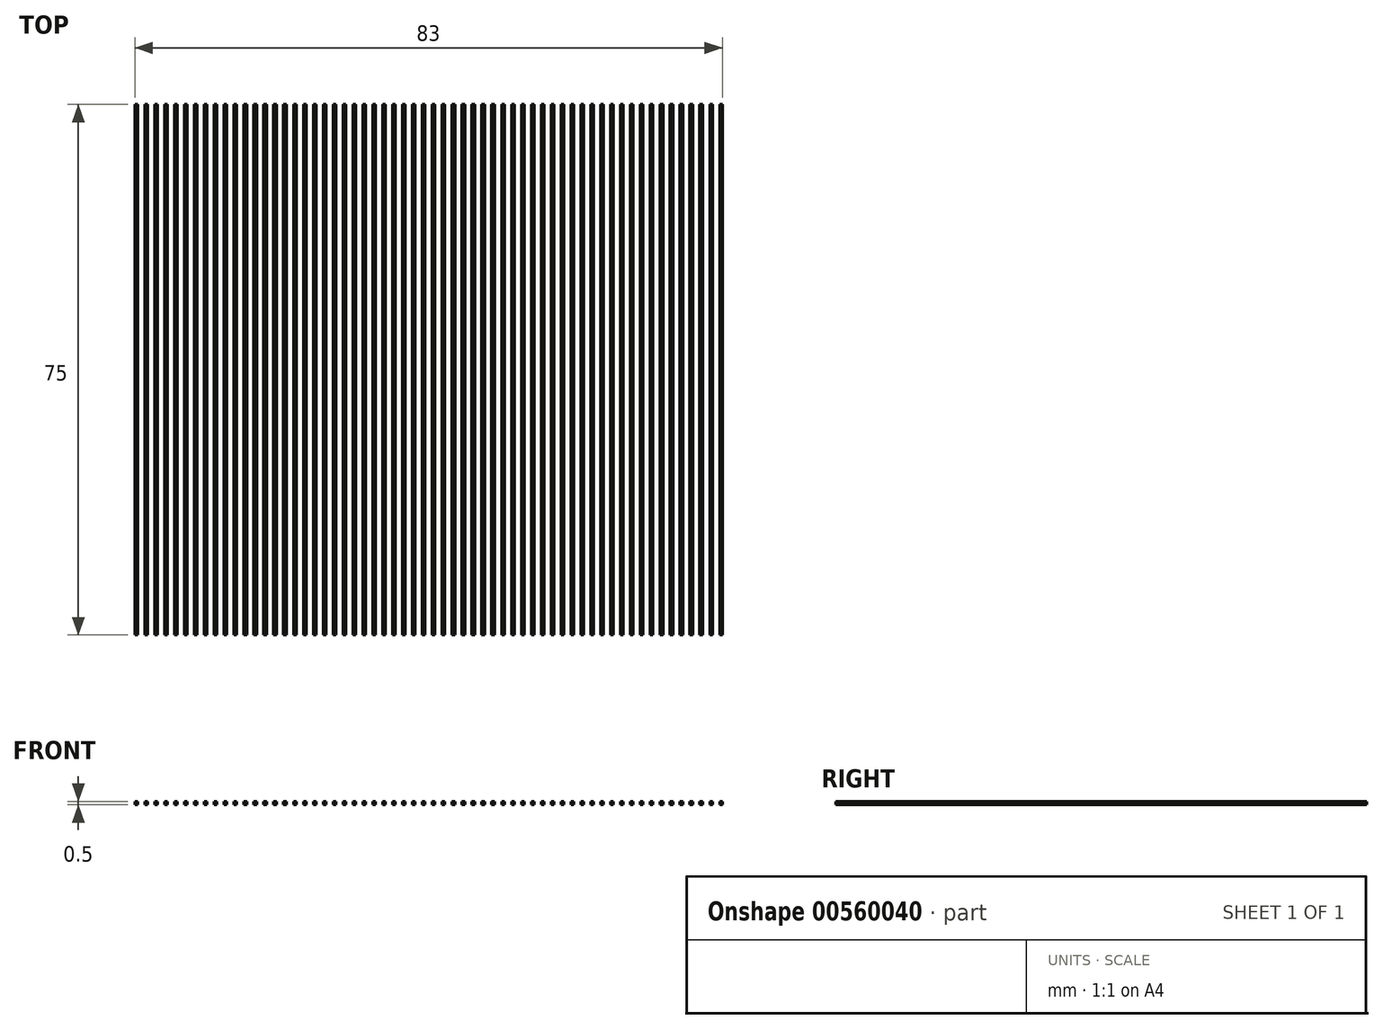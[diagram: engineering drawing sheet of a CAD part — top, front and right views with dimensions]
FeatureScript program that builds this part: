
annotation { "Feature Type Name" : "Feature", "Feature Type Description" : "" }
export const myFeature = defineFeature(function(context is Context, id is Id, definition is map)
    precondition{}
    {
        {
            var Q0;
            Q0=qCreatedBy(makeId("Top.planeOp"),FACE);
            var sketch = newSketch(context, id + "F0", { "sketchPlane" : qUnion([Q0])});
            skLineSegment(sketch, "E0.bottom", {"start": v(-41.94, 37.5) * mm, "end": v(-42.34, 37.5) * mm});
            skLineSegment(sketch, "E0.top", {"start": v(-41.94, -37.5) * mm, "end": v(-42.34, -37.5) * mm});
            skLineSegment(sketch, "E0.left", {"start": v(-41.94, 37.5) * mm, "end": v(-41.94, -37.5) * mm});
            skLineSegment(sketch, "E0.right", {"start": v(-42.34, 37.5) * mm, "end": v(-42.34, -37.5) * mm});
            skPoint(sketch, "E0.middle", {"position": v(-42.14, 0) * mm});
            skLineSegment(sketch, "E1.1.0.0", {"start": v(-40.94, 37.5) * mm, "end": v(-40.94, -37.5) * mm});
            skPoint(sketch, "E1.1.0.1", {"position": v(-40.74, 0) * mm});
            skLineSegment(sketch, "E1.1.0.2", {"start": v(-40.54, 37.5) * mm, "end": v(-40.54, -37.5) * mm});
            skLineSegment(sketch, "E1.1.0.3", {"start": v(-40.54, -37.5) * mm, "end": v(-40.94, -37.5) * mm});
            skLineSegment(sketch, "E1.1.0.4", {"start": v(-40.54, 37.5) * mm, "end": v(-40.94, 37.5) * mm});
            skLineSegment(sketch, "E1.2.0.0", {"start": v(-39.54, 37.5) * mm, "end": v(-39.54, -37.5) * mm});
            skPoint(sketch, "E1.2.0.1", {"position": v(-39.34, 0) * mm});
            skLineSegment(sketch, "E1.2.0.2", {"start": v(-39.14, 37.5) * mm, "end": v(-39.14, -37.5) * mm});
            skLineSegment(sketch, "E1.2.0.3", {"start": v(-39.14, -37.5) * mm, "end": v(-39.54, -37.5) * mm});
            skLineSegment(sketch, "E1.2.0.4", {"start": v(-39.14, 37.5) * mm, "end": v(-39.54, 37.5) * mm});
            skLineSegment(sketch, "E1.3.0.0", {"start": v(-38.14, 37.5) * mm, "end": v(-38.14, -37.5) * mm});
            skPoint(sketch, "E1.3.0.1", {"position": v(-37.94, 0) * mm});
            skLineSegment(sketch, "E1.3.0.2", {"start": v(-37.74, 37.5) * mm, "end": v(-37.74, -37.5) * mm});
            skLineSegment(sketch, "E1.3.0.3", {"start": v(-37.74, -37.5) * mm, "end": v(-38.14, -37.5) * mm});
            skLineSegment(sketch, "E1.3.0.4", {"start": v(-37.74, 37.5) * mm, "end": v(-38.14, 37.5) * mm});
            skLineSegment(sketch, "E1.4.0.0", {"start": v(-36.74, 37.5) * mm, "end": v(-36.74, -37.5) * mm});
            skPoint(sketch, "E1.4.0.1", {"position": v(-36.54, 0) * mm});
            skLineSegment(sketch, "E1.4.0.2", {"start": v(-36.34, 37.5) * mm, "end": v(-36.34, -37.5) * mm});
            skLineSegment(sketch, "E1.4.0.3", {"start": v(-36.34, -37.5) * mm, "end": v(-36.74, -37.5) * mm});
            skLineSegment(sketch, "E1.4.0.4", {"start": v(-36.34, 37.5) * mm, "end": v(-36.74, 37.5) * mm});
            skLineSegment(sketch, "E1.5.0.0", {"start": v(-35.34, 37.5) * mm, "end": v(-35.34, -37.5) * mm});
            skPoint(sketch, "E1.5.0.1", {"position": v(-35.14, 0) * mm});
            skLineSegment(sketch, "E1.5.0.2", {"start": v(-34.94, 37.5) * mm, "end": v(-34.94, -37.5) * mm});
            skLineSegment(sketch, "E1.5.0.3", {"start": v(-34.94, -37.5) * mm, "end": v(-35.34, -37.5) * mm});
            skLineSegment(sketch, "E1.5.0.4", {"start": v(-34.94, 37.5) * mm, "end": v(-35.34, 37.5) * mm});
            skLineSegment(sketch, "E1.6.0.0", {"start": v(-33.94, 37.5) * mm, "end": v(-33.94, -37.5) * mm});
            skPoint(sketch, "E1.6.0.1", {"position": v(-33.74, 0) * mm});
            skLineSegment(sketch, "E1.6.0.2", {"start": v(-33.54, 37.5) * mm, "end": v(-33.54, -37.5) * mm});
            skLineSegment(sketch, "E1.6.0.3", {"start": v(-33.54, -37.5) * mm, "end": v(-33.94, -37.5) * mm});
            skLineSegment(sketch, "E1.6.0.4", {"start": v(-33.54, 37.5) * mm, "end": v(-33.94, 37.5) * mm});
            skLineSegment(sketch, "E1.7.0.0", {"start": v(-32.54, 37.5) * mm, "end": v(-32.54, -37.5) * mm});
            skPoint(sketch, "E1.7.0.1", {"position": v(-32.34, 0) * mm});
            skLineSegment(sketch, "E1.7.0.2", {"start": v(-32.14, 37.5) * mm, "end": v(-32.14, -37.5) * mm});
            skLineSegment(sketch, "E1.7.0.3", {"start": v(-32.14, -37.5) * mm, "end": v(-32.54, -37.5) * mm});
            skLineSegment(sketch, "E1.7.0.4", {"start": v(-32.14, 37.5) * mm, "end": v(-32.54, 37.5) * mm});
            skLineSegment(sketch, "E1.8.0.0", {"start": v(-31.14, 37.5) * mm, "end": v(-31.14, -37.5) * mm});
            skPoint(sketch, "E1.8.0.1", {"position": v(-30.94, 0) * mm});
            skLineSegment(sketch, "E1.8.0.2", {"start": v(-30.74, 37.5) * mm, "end": v(-30.74, -37.5) * mm});
            skLineSegment(sketch, "E1.8.0.3", {"start": v(-30.74, -37.5) * mm, "end": v(-31.14, -37.5) * mm});
            skLineSegment(sketch, "E1.8.0.4", {"start": v(-30.74, 37.5) * mm, "end": v(-31.14, 37.5) * mm});
            skLineSegment(sketch, "E1.9.0.0", {"start": v(-29.74, 37.5) * mm, "end": v(-29.74, -37.5) * mm});
            skPoint(sketch, "E1.9.0.1", {"position": v(-29.54, 0) * mm});
            skLineSegment(sketch, "E1.9.0.2", {"start": v(-29.34, 37.5) * mm, "end": v(-29.34, -37.5) * mm});
            skLineSegment(sketch, "E1.9.0.3", {"start": v(-29.34, -37.5) * mm, "end": v(-29.74, -37.5) * mm});
            skLineSegment(sketch, "E1.9.0.4", {"start": v(-29.34, 37.5) * mm, "end": v(-29.74, 37.5) * mm});
            skLineSegment(sketch, "E1.10.0.0", {"start": v(-28.34, 37.5) * mm, "end": v(-28.34, -37.5) * mm});
            skPoint(sketch, "E1.10.0.1", {"position": v(-28.14, 0) * mm});
            skLineSegment(sketch, "E1.10.0.2", {"start": v(-27.94, 37.5) * mm, "end": v(-27.94, -37.5) * mm});
            skLineSegment(sketch, "E1.10.0.3", {"start": v(-27.94, -37.5) * mm, "end": v(-28.34, -37.5) * mm});
            skLineSegment(sketch, "E1.10.0.4", {"start": v(-27.94, 37.5) * mm, "end": v(-28.34, 37.5) * mm});
            skLineSegment(sketch, "E1.11.0.0", {"start": v(-26.94, 37.5) * mm, "end": v(-26.94, -37.5) * mm});
            skPoint(sketch, "E1.11.0.1", {"position": v(-26.74, 0) * mm});
            skLineSegment(sketch, "E1.11.0.2", {"start": v(-26.54, 37.5) * mm, "end": v(-26.54, -37.5) * mm});
            skLineSegment(sketch, "E1.11.0.3", {"start": v(-26.54, -37.5) * mm, "end": v(-26.94, -37.5) * mm});
            skLineSegment(sketch, "E1.11.0.4", {"start": v(-26.54, 37.5) * mm, "end": v(-26.94, 37.5) * mm});
            skLineSegment(sketch, "E1.12.0.0", {"start": v(-25.54, 37.5) * mm, "end": v(-25.54, -37.5) * mm});
            skPoint(sketch, "E1.12.0.1", {"position": v(-25.34, 0) * mm});
            skLineSegment(sketch, "E1.12.0.2", {"start": v(-25.14, 37.5) * mm, "end": v(-25.14, -37.5) * mm});
            skLineSegment(sketch, "E1.12.0.3", {"start": v(-25.14, -37.5) * mm, "end": v(-25.54, -37.5) * mm});
            skLineSegment(sketch, "E1.12.0.4", {"start": v(-25.14, 37.5) * mm, "end": v(-25.54, 37.5) * mm});
            skLineSegment(sketch, "E1.13.0.0", {"start": v(-24.14, 37.5) * mm, "end": v(-24.14, -37.5) * mm});
            skPoint(sketch, "E1.13.0.1", {"position": v(-23.94, 0) * mm});
            skLineSegment(sketch, "E1.13.0.2", {"start": v(-23.74, 37.5) * mm, "end": v(-23.74, -37.5) * mm});
            skLineSegment(sketch, "E1.13.0.3", {"start": v(-23.74, -37.5) * mm, "end": v(-24.14, -37.5) * mm});
            skLineSegment(sketch, "E1.13.0.4", {"start": v(-23.74, 37.5) * mm, "end": v(-24.14, 37.5) * mm});
            skLineSegment(sketch, "E1.14.0.0", {"start": v(-22.74, 37.5) * mm, "end": v(-22.74, -37.5) * mm});
            skPoint(sketch, "E1.14.0.1", {"position": v(-22.54, 0) * mm});
            skLineSegment(sketch, "E1.14.0.2", {"start": v(-22.34, 37.5) * mm, "end": v(-22.34, -37.5) * mm});
            skLineSegment(sketch, "E1.14.0.3", {"start": v(-22.34, -37.5) * mm, "end": v(-22.74, -37.5) * mm});
            skLineSegment(sketch, "E1.14.0.4", {"start": v(-22.34, 37.5) * mm, "end": v(-22.74, 37.5) * mm});
            skLineSegment(sketch, "E1.15.0.0", {"start": v(-21.34, 37.5) * mm, "end": v(-21.34, -37.5) * mm});
            skPoint(sketch, "E1.15.0.1", {"position": v(-21.14, 0) * mm});
            skLineSegment(sketch, "E1.15.0.2", {"start": v(-20.94, 37.5) * mm, "end": v(-20.94, -37.5) * mm});
            skLineSegment(sketch, "E1.15.0.3", {"start": v(-20.94, -37.5) * mm, "end": v(-21.34, -37.5) * mm});
            skLineSegment(sketch, "E1.15.0.4", {"start": v(-20.94, 37.5) * mm, "end": v(-21.34, 37.5) * mm});
            skLineSegment(sketch, "E1.16.0.0", {"start": v(-19.94, 37.5) * mm, "end": v(-19.94, -37.5) * mm});
            skPoint(sketch, "E1.16.0.1", {"position": v(-19.74, 0) * mm});
            skLineSegment(sketch, "E1.16.0.2", {"start": v(-19.54, 37.5) * mm, "end": v(-19.54, -37.5) * mm});
            skLineSegment(sketch, "E1.16.0.3", {"start": v(-19.54, -37.5) * mm, "end": v(-19.94, -37.5) * mm});
            skLineSegment(sketch, "E1.16.0.4", {"start": v(-19.54, 37.5) * mm, "end": v(-19.94, 37.5) * mm});
            skLineSegment(sketch, "E1.17.0.0", {"start": v(-18.54, 37.5) * mm, "end": v(-18.54, -37.5) * mm});
            skPoint(sketch, "E1.17.0.1", {"position": v(-18.34, 0) * mm});
            skLineSegment(sketch, "E1.17.0.2", {"start": v(-18.14, 37.5) * mm, "end": v(-18.14, -37.5) * mm});
            skLineSegment(sketch, "E1.17.0.3", {"start": v(-18.14, -37.5) * mm, "end": v(-18.54, -37.5) * mm});
            skLineSegment(sketch, "E1.17.0.4", {"start": v(-18.14, 37.5) * mm, "end": v(-18.54, 37.5) * mm});
            skLineSegment(sketch, "E1.18.0.0", {"start": v(-17.14, 37.5) * mm, "end": v(-17.14, -37.5) * mm});
            skPoint(sketch, "E1.18.0.1", {"position": v(-16.94, 0) * mm});
            skLineSegment(sketch, "E1.18.0.2", {"start": v(-16.74, 37.5) * mm, "end": v(-16.74, -37.5) * mm});
            skLineSegment(sketch, "E1.18.0.3", {"start": v(-16.74, -37.5) * mm, "end": v(-17.14, -37.5) * mm});
            skLineSegment(sketch, "E1.18.0.4", {"start": v(-16.74, 37.5) * mm, "end": v(-17.14, 37.5) * mm});
            skLineSegment(sketch, "E1.19.0.0", {"start": v(-15.74, 37.5) * mm, "end": v(-15.74, -37.5) * mm});
            skPoint(sketch, "E1.19.0.1", {"position": v(-15.54, 0) * mm});
            skLineSegment(sketch, "E1.19.0.2", {"start": v(-15.34, 37.5) * mm, "end": v(-15.34, -37.5) * mm});
            skLineSegment(sketch, "E1.19.0.3", {"start": v(-15.34, -37.5) * mm, "end": v(-15.74, -37.5) * mm});
            skLineSegment(sketch, "E1.19.0.4", {"start": v(-15.34, 37.5) * mm, "end": v(-15.74, 37.5) * mm});
            skLineSegment(sketch, "E1.20.0.0", {"start": v(-14.34, 37.5) * mm, "end": v(-14.34, -37.5) * mm});
            skPoint(sketch, "E1.20.0.1", {"position": v(-14.14, 0) * mm});
            skLineSegment(sketch, "E1.20.0.2", {"start": v(-13.94, 37.5) * mm, "end": v(-13.94, -37.5) * mm});
            skLineSegment(sketch, "E1.20.0.3", {"start": v(-13.94, -37.5) * mm, "end": v(-14.34, -37.5) * mm});
            skLineSegment(sketch, "E1.20.0.4", {"start": v(-13.94, 37.5) * mm, "end": v(-14.34, 37.5) * mm});
            skLineSegment(sketch, "E1.21.0.0", {"start": v(-12.94, 37.5) * mm, "end": v(-12.94, -37.5) * mm});
            skPoint(sketch, "E1.21.0.1", {"position": v(-12.74, 0) * mm});
            skLineSegment(sketch, "E1.21.0.2", {"start": v(-12.54, 37.5) * mm, "end": v(-12.54, -37.5) * mm});
            skLineSegment(sketch, "E1.21.0.3", {"start": v(-12.54, -37.5) * mm, "end": v(-12.94, -37.5) * mm});
            skLineSegment(sketch, "E1.21.0.4", {"start": v(-12.54, 37.5) * mm, "end": v(-12.94, 37.5) * mm});
            skLineSegment(sketch, "E1.22.0.0", {"start": v(-11.54, 37.5) * mm, "end": v(-11.54, -37.5) * mm});
            skPoint(sketch, "E1.22.0.1", {"position": v(-11.34, 0) * mm});
            skLineSegment(sketch, "E1.22.0.2", {"start": v(-11.14, 37.5) * mm, "end": v(-11.14, -37.5) * mm});
            skLineSegment(sketch, "E1.22.0.3", {"start": v(-11.14, -37.5) * mm, "end": v(-11.54, -37.5) * mm});
            skLineSegment(sketch, "E1.22.0.4", {"start": v(-11.14, 37.5) * mm, "end": v(-11.54, 37.5) * mm});
            skLineSegment(sketch, "E1.23.0.0", {"start": v(-10.14, 37.5) * mm, "end": v(-10.14, -37.5) * mm});
            skPoint(sketch, "E1.23.0.1", {"position": v(-9.94, 0) * mm});
            skLineSegment(sketch, "E1.23.0.2", {"start": v(-9.74, 37.5) * mm, "end": v(-9.74, -37.5) * mm});
            skLineSegment(sketch, "E1.23.0.3", {"start": v(-9.74, -37.5) * mm, "end": v(-10.14, -37.5) * mm});
            skLineSegment(sketch, "E1.23.0.4", {"start": v(-9.74, 37.5) * mm, "end": v(-10.14, 37.5) * mm});
            skLineSegment(sketch, "E1.24.0.0", {"start": v(-8.74, 37.5) * mm, "end": v(-8.74, -37.5) * mm});
            skPoint(sketch, "E1.24.0.1", {"position": v(-8.54, 0) * mm});
            skLineSegment(sketch, "E1.24.0.2", {"start": v(-8.34, 37.5) * mm, "end": v(-8.34, -37.5) * mm});
            skLineSegment(sketch, "E1.24.0.3", {"start": v(-8.34, -37.5) * mm, "end": v(-8.74, -37.5) * mm});
            skLineSegment(sketch, "E1.24.0.4", {"start": v(-8.34, 37.5) * mm, "end": v(-8.74, 37.5) * mm});
            skLineSegment(sketch, "E1.25.0.0", {"start": v(-7.34, 37.5) * mm, "end": v(-7.34, -37.5) * mm});
            skPoint(sketch, "E1.25.0.1", {"position": v(-7.14, 0) * mm});
            skLineSegment(sketch, "E1.25.0.2", {"start": v(-6.94, 37.5) * mm, "end": v(-6.94, -37.5) * mm});
            skLineSegment(sketch, "E1.25.0.3", {"start": v(-6.94, -37.5) * mm, "end": v(-7.34, -37.5) * mm});
            skLineSegment(sketch, "E1.25.0.4", {"start": v(-6.94, 37.5) * mm, "end": v(-7.34, 37.5) * mm});
            skLineSegment(sketch, "E1.26.0.0", {"start": v(-5.94, 37.5) * mm, "end": v(-5.94, -37.5) * mm});
            skPoint(sketch, "E1.26.0.1", {"position": v(-5.74, 0) * mm});
            skLineSegment(sketch, "E1.26.0.2", {"start": v(-5.54, 37.5) * mm, "end": v(-5.54, -37.5) * mm});
            skLineSegment(sketch, "E1.26.0.3", {"start": v(-5.54, -37.5) * mm, "end": v(-5.94, -37.5) * mm});
            skLineSegment(sketch, "E1.26.0.4", {"start": v(-5.54, 37.5) * mm, "end": v(-5.94, 37.5) * mm});
            skLineSegment(sketch, "E1.27.0.0", {"start": v(-4.54, 37.5) * mm, "end": v(-4.54, -37.5) * mm});
            skPoint(sketch, "E1.27.0.1", {"position": v(-4.34, 0) * mm});
            skLineSegment(sketch, "E1.27.0.2", {"start": v(-4.14, 37.5) * mm, "end": v(-4.14, -37.5) * mm});
            skLineSegment(sketch, "E1.27.0.3", {"start": v(-4.14, -37.5) * mm, "end": v(-4.54, -37.5) * mm});
            skLineSegment(sketch, "E1.27.0.4", {"start": v(-4.14, 37.5) * mm, "end": v(-4.54, 37.5) * mm});
            skLineSegment(sketch, "E1.28.0.0", {"start": v(-3.14, 37.5) * mm, "end": v(-3.14, -37.5) * mm});
            skPoint(sketch, "E1.28.0.1", {"position": v(-2.94, 0) * mm});
            skLineSegment(sketch, "E1.28.0.2", {"start": v(-2.74, 37.5) * mm, "end": v(-2.74, -37.5) * mm});
            skLineSegment(sketch, "E1.28.0.3", {"start": v(-2.74, -37.5) * mm, "end": v(-3.14, -37.5) * mm});
            skLineSegment(sketch, "E1.28.0.4", {"start": v(-2.74, 37.5) * mm, "end": v(-3.14, 37.5) * mm});
            skLineSegment(sketch, "E1.29.0.0", {"start": v(-1.74, 37.5) * mm, "end": v(-1.74, -37.5) * mm});
            skPoint(sketch, "E1.29.0.1", {"position": v(-1.54, 0) * mm});
            skLineSegment(sketch, "E1.29.0.2", {"start": v(-1.34, 37.5) * mm, "end": v(-1.34, -37.5) * mm});
            skLineSegment(sketch, "E1.29.0.3", {"start": v(-1.34, -37.5) * mm, "end": v(-1.74, -37.5) * mm});
            skLineSegment(sketch, "E1.29.0.4", {"start": v(-1.34, 37.5) * mm, "end": v(-1.74, 37.5) * mm});
            skLineSegment(sketch, "E1.30.0.0", {"start": v(-0.34, 37.5) * mm, "end": v(-0.34, -37.5) * mm});
            skPoint(sketch, "E1.30.0.1", {"position": v(-0.14, 0) * mm});
            skLineSegment(sketch, "E1.30.0.2", {"start": v(0.06, 37.5) * mm, "end": v(0.06, -37.5) * mm});
            skLineSegment(sketch, "E1.30.0.3", {"start": v(0.06, -37.5) * mm, "end": v(-0.34, -37.5) * mm});
            skLineSegment(sketch, "E1.30.0.4", {"start": v(0.06, 37.5) * mm, "end": v(-0.34, 37.5) * mm});
            skLineSegment(sketch, "E1.31.0.0", {"start": v(1.06, 37.5) * mm, "end": v(1.06, -37.5) * mm});
            skPoint(sketch, "E1.31.0.1", {"position": v(1.26, 0) * mm});
            skLineSegment(sketch, "E1.31.0.2", {"start": v(1.46, 37.5) * mm, "end": v(1.46, -37.5) * mm});
            skLineSegment(sketch, "E1.31.0.3", {"start": v(1.46, -37.5) * mm, "end": v(1.06, -37.5) * mm});
            skLineSegment(sketch, "E1.31.0.4", {"start": v(1.46, 37.5) * mm, "end": v(1.06, 37.5) * mm});
            skLineSegment(sketch, "E1.32.0.0", {"start": v(2.46, 37.5) * mm, "end": v(2.46, -37.5) * mm});
            skPoint(sketch, "E1.32.0.1", {"position": v(2.66, 0) * mm});
            skLineSegment(sketch, "E1.32.0.2", {"start": v(2.86, 37.5) * mm, "end": v(2.86, -37.5) * mm});
            skLineSegment(sketch, "E1.32.0.3", {"start": v(2.86, -37.5) * mm, "end": v(2.46, -37.5) * mm});
            skLineSegment(sketch, "E1.32.0.4", {"start": v(2.86, 37.5) * mm, "end": v(2.46, 37.5) * mm});
            skLineSegment(sketch, "E1.33.0.0", {"start": v(3.86, 37.5) * mm, "end": v(3.86, -37.5) * mm});
            skPoint(sketch, "E1.33.0.1", {"position": v(4.06, 0) * mm});
            skLineSegment(sketch, "E1.33.0.2", {"start": v(4.26, 37.5) * mm, "end": v(4.26, -37.5) * mm});
            skLineSegment(sketch, "E1.33.0.3", {"start": v(4.26, -37.5) * mm, "end": v(3.86, -37.5) * mm});
            skLineSegment(sketch, "E1.33.0.4", {"start": v(4.26, 37.5) * mm, "end": v(3.86, 37.5) * mm});
            skLineSegment(sketch, "E1.34.0.0", {"start": v(5.26, 37.5) * mm, "end": v(5.26, -37.5) * mm});
            skPoint(sketch, "E1.34.0.1", {"position": v(5.46, 0) * mm});
            skLineSegment(sketch, "E1.34.0.2", {"start": v(5.66, 37.5) * mm, "end": v(5.66, -37.5) * mm});
            skLineSegment(sketch, "E1.34.0.3", {"start": v(5.66, -37.5) * mm, "end": v(5.26, -37.5) * mm});
            skLineSegment(sketch, "E1.34.0.4", {"start": v(5.66, 37.5) * mm, "end": v(5.26, 37.5) * mm});
            skLineSegment(sketch, "E1.35.0.0", {"start": v(6.66, 37.5) * mm, "end": v(6.66, -37.5) * mm});
            skPoint(sketch, "E1.35.0.1", {"position": v(6.86, 0) * mm});
            skLineSegment(sketch, "E1.35.0.2", {"start": v(7.06, 37.5) * mm, "end": v(7.06, -37.5) * mm});
            skLineSegment(sketch, "E1.35.0.3", {"start": v(7.06, -37.5) * mm, "end": v(6.66, -37.5) * mm});
            skLineSegment(sketch, "E1.35.0.4", {"start": v(7.06, 37.5) * mm, "end": v(6.66, 37.5) * mm});
            skLineSegment(sketch, "E1.36.0.0", {"start": v(8.06, 37.5) * mm, "end": v(8.06, -37.5) * mm});
            skPoint(sketch, "E1.36.0.1", {"position": v(8.26, 0) * mm});
            skLineSegment(sketch, "E1.36.0.2", {"start": v(8.46, 37.5) * mm, "end": v(8.46, -37.5) * mm});
            skLineSegment(sketch, "E1.36.0.3", {"start": v(8.46, -37.5) * mm, "end": v(8.06, -37.5) * mm});
            skLineSegment(sketch, "E1.36.0.4", {"start": v(8.46, 37.5) * mm, "end": v(8.06, 37.5) * mm});
            skLineSegment(sketch, "E1.37.0.0", {"start": v(9.46, 37.5) * mm, "end": v(9.46, -37.5) * mm});
            skPoint(sketch, "E1.37.0.1", {"position": v(9.66, 0) * mm});
            skLineSegment(sketch, "E1.37.0.2", {"start": v(9.86, 37.5) * mm, "end": v(9.86, -37.5) * mm});
            skLineSegment(sketch, "E1.37.0.3", {"start": v(9.86, -37.5) * mm, "end": v(9.46, -37.5) * mm});
            skLineSegment(sketch, "E1.37.0.4", {"start": v(9.86, 37.5) * mm, "end": v(9.46, 37.5) * mm});
            skLineSegment(sketch, "E1.38.0.0", {"start": v(10.86, 37.5) * mm, "end": v(10.86, -37.5) * mm});
            skPoint(sketch, "E1.38.0.1", {"position": v(11.06, 0) * mm});
            skLineSegment(sketch, "E1.38.0.2", {"start": v(11.26, 37.5) * mm, "end": v(11.26, -37.5) * mm});
            skLineSegment(sketch, "E1.38.0.3", {"start": v(11.26, -37.5) * mm, "end": v(10.86, -37.5) * mm});
            skLineSegment(sketch, "E1.38.0.4", {"start": v(11.26, 37.5) * mm, "end": v(10.86, 37.5) * mm});
            skLineSegment(sketch, "E1.39.0.0", {"start": v(12.26, 37.5) * mm, "end": v(12.26, -37.5) * mm});
            skPoint(sketch, "E1.39.0.1", {"position": v(12.46, 0) * mm});
            skLineSegment(sketch, "E1.39.0.2", {"start": v(12.66, 37.5) * mm, "end": v(12.66, -37.5) * mm});
            skLineSegment(sketch, "E1.39.0.3", {"start": v(12.66, -37.5) * mm, "end": v(12.26, -37.5) * mm});
            skLineSegment(sketch, "E1.39.0.4", {"start": v(12.66, 37.5) * mm, "end": v(12.26, 37.5) * mm});
            skLineSegment(sketch, "E1.40.0.0", {"start": v(13.66, 37.5) * mm, "end": v(13.66, -37.5) * mm});
            skPoint(sketch, "E1.40.0.1", {"position": v(13.86, 0) * mm});
            skLineSegment(sketch, "E1.40.0.2", {"start": v(14.06, 37.5) * mm, "end": v(14.06, -37.5) * mm});
            skLineSegment(sketch, "E1.40.0.3", {"start": v(14.06, -37.5) * mm, "end": v(13.66, -37.5) * mm});
            skLineSegment(sketch, "E1.40.0.4", {"start": v(14.06, 37.5) * mm, "end": v(13.66, 37.5) * mm});
            skLineSegment(sketch, "E1.41.0.0", {"start": v(15.06, 37.5) * mm, "end": v(15.06, -37.5) * mm});
            skPoint(sketch, "E1.41.0.1", {"position": v(15.26, 0) * mm});
            skLineSegment(sketch, "E1.41.0.2", {"start": v(15.46, 37.5) * mm, "end": v(15.46, -37.5) * mm});
            skLineSegment(sketch, "E1.41.0.3", {"start": v(15.46, -37.5) * mm, "end": v(15.06, -37.5) * mm});
            skLineSegment(sketch, "E1.41.0.4", {"start": v(15.46, 37.5) * mm, "end": v(15.06, 37.5) * mm});
            skLineSegment(sketch, "E1.42.0.0", {"start": v(16.46, 37.5) * mm, "end": v(16.46, -37.5) * mm});
            skPoint(sketch, "E1.42.0.1", {"position": v(16.66, 0) * mm});
            skLineSegment(sketch, "E1.42.0.2", {"start": v(16.86, 37.5) * mm, "end": v(16.86, -37.5) * mm});
            skLineSegment(sketch, "E1.42.0.3", {"start": v(16.86, -37.5) * mm, "end": v(16.46, -37.5) * mm});
            skLineSegment(sketch, "E1.42.0.4", {"start": v(16.86, 37.5) * mm, "end": v(16.46, 37.5) * mm});
            skLineSegment(sketch, "E1.43.0.0", {"start": v(17.86, 37.5) * mm, "end": v(17.86, -37.5) * mm});
            skPoint(sketch, "E1.43.0.1", {"position": v(18.06, 0) * mm});
            skLineSegment(sketch, "E1.43.0.2", {"start": v(18.26, 37.5) * mm, "end": v(18.26, -37.5) * mm});
            skLineSegment(sketch, "E1.43.0.3", {"start": v(18.26, -37.5) * mm, "end": v(17.86, -37.5) * mm});
            skLineSegment(sketch, "E1.43.0.4", {"start": v(18.26, 37.5) * mm, "end": v(17.86, 37.5) * mm});
            skLineSegment(sketch, "E1.44.0.0", {"start": v(19.26, 37.5) * mm, "end": v(19.26, -37.5) * mm});
            skPoint(sketch, "E1.44.0.1", {"position": v(19.46, 0) * mm});
            skLineSegment(sketch, "E1.44.0.2", {"start": v(19.66, 37.5) * mm, "end": v(19.66, -37.5) * mm});
            skLineSegment(sketch, "E1.44.0.3", {"start": v(19.66, -37.5) * mm, "end": v(19.26, -37.5) * mm});
            skLineSegment(sketch, "E1.44.0.4", {"start": v(19.66, 37.5) * mm, "end": v(19.26, 37.5) * mm});
            skLineSegment(sketch, "E1.45.0.0", {"start": v(20.66, 37.5) * mm, "end": v(20.66, -37.5) * mm});
            skPoint(sketch, "E1.45.0.1", {"position": v(20.86, 0) * mm});
            skLineSegment(sketch, "E1.45.0.2", {"start": v(21.06, 37.5) * mm, "end": v(21.06, -37.5) * mm});
            skLineSegment(sketch, "E1.45.0.3", {"start": v(21.06, -37.5) * mm, "end": v(20.66, -37.5) * mm});
            skLineSegment(sketch, "E1.45.0.4", {"start": v(21.06, 37.5) * mm, "end": v(20.66, 37.5) * mm});
            skLineSegment(sketch, "E1.46.0.0", {"start": v(22.06, 37.5) * mm, "end": v(22.06, -37.5) * mm});
            skPoint(sketch, "E1.46.0.1", {"position": v(22.26, 0) * mm});
            skLineSegment(sketch, "E1.46.0.2", {"start": v(22.46, 37.5) * mm, "end": v(22.46, -37.5) * mm});
            skLineSegment(sketch, "E1.46.0.3", {"start": v(22.46, -37.5) * mm, "end": v(22.06, -37.5) * mm});
            skLineSegment(sketch, "E1.46.0.4", {"start": v(22.46, 37.5) * mm, "end": v(22.06, 37.5) * mm});
            skLineSegment(sketch, "E1.47.0.0", {"start": v(23.46, 37.5) * mm, "end": v(23.46, -37.5) * mm});
            skPoint(sketch, "E1.47.0.1", {"position": v(23.66, 0) * mm});
            skLineSegment(sketch, "E1.47.0.2", {"start": v(23.86, 37.5) * mm, "end": v(23.86, -37.5) * mm});
            skLineSegment(sketch, "E1.47.0.3", {"start": v(23.86, -37.5) * mm, "end": v(23.46, -37.5) * mm});
            skLineSegment(sketch, "E1.47.0.4", {"start": v(23.86, 37.5) * mm, "end": v(23.46, 37.5) * mm});
            skLineSegment(sketch, "E1.48.0.0", {"start": v(24.86, 37.5) * mm, "end": v(24.86, -37.5) * mm});
            skPoint(sketch, "E1.48.0.1", {"position": v(25.06, 0) * mm});
            skLineSegment(sketch, "E1.48.0.2", {"start": v(25.26, 37.5) * mm, "end": v(25.26, -37.5) * mm});
            skLineSegment(sketch, "E1.48.0.3", {"start": v(25.26, -37.5) * mm, "end": v(24.86, -37.5) * mm});
            skLineSegment(sketch, "E1.48.0.4", {"start": v(25.26, 37.5) * mm, "end": v(24.86, 37.5) * mm});
            skLineSegment(sketch, "E1.49.0.0", {"start": v(26.26, 37.5) * mm, "end": v(26.26, -37.5) * mm});
            skPoint(sketch, "E1.49.0.1", {"position": v(26.46, 0) * mm});
            skLineSegment(sketch, "E1.49.0.2", {"start": v(26.66, 37.5) * mm, "end": v(26.66, -37.5) * mm});
            skLineSegment(sketch, "E1.49.0.3", {"start": v(26.66, -37.5) * mm, "end": v(26.26, -37.5) * mm});
            skLineSegment(sketch, "E1.49.0.4", {"start": v(26.66, 37.5) * mm, "end": v(26.26, 37.5) * mm});
            skLineSegment(sketch, "E1.50.0.0", {"start": v(27.66, 37.5) * mm, "end": v(27.66, -37.5) * mm});
            skPoint(sketch, "E1.50.0.1", {"position": v(27.86, 0) * mm});
            skLineSegment(sketch, "E1.50.0.2", {"start": v(28.06, 37.5) * mm, "end": v(28.06, -37.5) * mm});
            skLineSegment(sketch, "E1.50.0.3", {"start": v(28.06, -37.5) * mm, "end": v(27.66, -37.5) * mm});
            skLineSegment(sketch, "E1.50.0.4", {"start": v(28.06, 37.5) * mm, "end": v(27.66, 37.5) * mm});
            skLineSegment(sketch, "E1.51.0.0", {"start": v(29.06, 37.5) * mm, "end": v(29.06, -37.5) * mm});
            skPoint(sketch, "E1.51.0.1", {"position": v(29.26, 0) * mm});
            skLineSegment(sketch, "E1.51.0.2", {"start": v(29.46, 37.5) * mm, "end": v(29.46, -37.5) * mm});
            skLineSegment(sketch, "E1.51.0.3", {"start": v(29.46, -37.5) * mm, "end": v(29.06, -37.5) * mm});
            skLineSegment(sketch, "E1.51.0.4", {"start": v(29.46, 37.5) * mm, "end": v(29.06, 37.5) * mm});
            skLineSegment(sketch, "E1.52.0.0", {"start": v(30.46, 37.5) * mm, "end": v(30.46, -37.5) * mm});
            skPoint(sketch, "E1.52.0.1", {"position": v(30.66, 0) * mm});
            skLineSegment(sketch, "E1.52.0.2", {"start": v(30.86, 37.5) * mm, "end": v(30.86, -37.5) * mm});
            skLineSegment(sketch, "E1.52.0.3", {"start": v(30.86, -37.5) * mm, "end": v(30.46, -37.5) * mm});
            skLineSegment(sketch, "E1.52.0.4", {"start": v(30.86, 37.5) * mm, "end": v(30.46, 37.5) * mm});
            skLineSegment(sketch, "E1.53.0.0", {"start": v(31.86, 37.5) * mm, "end": v(31.86, -37.5) * mm});
            skPoint(sketch, "E1.53.0.1", {"position": v(32.06, 0) * mm});
            skLineSegment(sketch, "E1.53.0.2", {"start": v(32.26, 37.5) * mm, "end": v(32.26, -37.5) * mm});
            skLineSegment(sketch, "E1.53.0.3", {"start": v(32.26, -37.5) * mm, "end": v(31.86, -37.5) * mm});
            skLineSegment(sketch, "E1.53.0.4", {"start": v(32.26, 37.5) * mm, "end": v(31.86, 37.5) * mm});
            skLineSegment(sketch, "E1.54.0.0", {"start": v(33.26, 37.5) * mm, "end": v(33.26, -37.5) * mm});
            skPoint(sketch, "E1.54.0.1", {"position": v(33.46, 0) * mm});
            skLineSegment(sketch, "E1.54.0.2", {"start": v(33.66, 37.5) * mm, "end": v(33.66, -37.5) * mm});
            skLineSegment(sketch, "E1.54.0.3", {"start": v(33.66, -37.5) * mm, "end": v(33.26, -37.5) * mm});
            skLineSegment(sketch, "E1.54.0.4", {"start": v(33.66, 37.5) * mm, "end": v(33.26, 37.5) * mm});
            skLineSegment(sketch, "E1.55.0.0", {"start": v(34.66, 37.5) * mm, "end": v(34.66, -37.5) * mm});
            skPoint(sketch, "E1.55.0.1", {"position": v(34.86, 0) * mm});
            skLineSegment(sketch, "E1.55.0.2", {"start": v(35.06, 37.5) * mm, "end": v(35.06, -37.5) * mm});
            skLineSegment(sketch, "E1.55.0.3", {"start": v(35.06, -37.5) * mm, "end": v(34.66, -37.5) * mm});
            skLineSegment(sketch, "E1.55.0.4", {"start": v(35.06, 37.5) * mm, "end": v(34.66, 37.5) * mm});
            skLineSegment(sketch, "E1.56.0.0", {"start": v(36.06, 37.5) * mm, "end": v(36.06, -37.5) * mm});
            skPoint(sketch, "E1.56.0.1", {"position": v(36.26, 0) * mm});
            skLineSegment(sketch, "E1.56.0.2", {"start": v(36.46, 37.5) * mm, "end": v(36.46, -37.5) * mm});
            skLineSegment(sketch, "E1.56.0.3", {"start": v(36.46, -37.5) * mm, "end": v(36.06, -37.5) * mm});
            skLineSegment(sketch, "E1.56.0.4", {"start": v(36.46, 37.5) * mm, "end": v(36.06, 37.5) * mm});
            skLineSegment(sketch, "E1.57.0.0", {"start": v(37.46, 37.5) * mm, "end": v(37.46, -37.5) * mm});
            skPoint(sketch, "E1.57.0.1", {"position": v(37.66, 0) * mm});
            skLineSegment(sketch, "E1.57.0.2", {"start": v(37.86, 37.5) * mm, "end": v(37.86, -37.5) * mm});
            skLineSegment(sketch, "E1.57.0.3", {"start": v(37.86, -37.5) * mm, "end": v(37.46, -37.5) * mm});
            skLineSegment(sketch, "E1.57.0.4", {"start": v(37.86, 37.5) * mm, "end": v(37.46, 37.5) * mm});
            skLineSegment(sketch, "E1.58.0.0", {"start": v(38.86, 37.5) * mm, "end": v(38.86, -37.5) * mm});
            skPoint(sketch, "E1.58.0.1", {"position": v(39.06, 0) * mm});
            skLineSegment(sketch, "E1.58.0.2", {"start": v(39.26, 37.5) * mm, "end": v(39.26, -37.5) * mm});
            skLineSegment(sketch, "E1.58.0.3", {"start": v(39.26, -37.5) * mm, "end": v(38.86, -37.5) * mm});
            skLineSegment(sketch, "E1.58.0.4", {"start": v(39.26, 37.5) * mm, "end": v(38.86, 37.5) * mm});
            skLineSegment(sketch, "E1.59.0.0", {"start": v(40.26, 37.5) * mm, "end": v(40.26, -37.5) * mm});
            skPoint(sketch, "E1.59.0.1", {"position": v(40.46, 0) * mm});
            skLineSegment(sketch, "E1.59.0.2", {"start": v(40.66, 37.5) * mm, "end": v(40.66, -37.5) * mm});
            skLineSegment(sketch, "E1.59.0.3", {"start": v(40.66, -37.5) * mm, "end": v(40.26, -37.5) * mm});
            skLineSegment(sketch, "E1.59.0.4", {"start": v(40.66, 37.5) * mm, "end": v(40.26, 37.5) * mm});
            skLineSegment(sketch, "E1.direction1", {"start": v(-42.34, -37.5) * mm, "end": v(-40.94, -37.5) * mm, "construction": true});
            skSolve(sketch);
        }
        {
            var Q0;
            Q0=makeQuery(id+"F0.imprint","IMPRINT",FACE,{"disambiguationData":[TD([[makeQuery(id+"F0.imprint","IMPRINT",EDGE,{"derivedFrom":sQuery(id+"F0.wireOp",EDGE,"E1.26.0.0")}),1.0]])]});
            var Q1;
            Q1=makeQuery(id+"F0.imprint","IMPRINT",FACE,{"disambiguationData":[TD([[makeQuery(id+"F0.imprint","IMPRINT",EDGE,{"derivedFrom":sQuery(id+"F0.wireOp",EDGE,"E1.43.0.0")}),1.0]])]});
            var Q2;
            Q2=makeQuery(id+"F0.imprint","IMPRINT",FACE,{"disambiguationData":[TD([[makeQuery(id+"F0.imprint","IMPRINT",EDGE,{"derivedFrom":sQuery(id+"F0.wireOp",EDGE,"E1.28.0.0")}),1.0]])]});
            var Q3;
            Q3=makeQuery(id+"F0.imprint","IMPRINT",FACE,{"disambiguationData":[TD([[makeQuery(id+"F0.imprint","IMPRINT",EDGE,{"derivedFrom":sQuery(id+"F0.wireOp",EDGE,"E1.44.0.0")}),1.0]])]});
            var Q4;
            Q4=makeQuery(id+"F0.imprint","IMPRINT",FACE,{"disambiguationData":[TD([[makeQuery(id+"F0.imprint","IMPRINT",EDGE,{"derivedFrom":sQuery(id+"F0.wireOp",EDGE,"E1.59.0.0")}),1.0]])]});
            var Q5;
            Q5=makeQuery(id+"F0.imprint","IMPRINT",FACE,{"disambiguationData":[TD([[makeQuery(id+"F0.imprint","IMPRINT",EDGE,{"derivedFrom":sQuery(id+"F0.wireOp",EDGE,"E1.27.0.0")}),1.0]])]});
            var Q6;
            Q6=makeQuery(id+"F0.imprint","IMPRINT",FACE,{"disambiguationData":[TD([[makeQuery(id+"F0.imprint","IMPRINT",EDGE,{"derivedFrom":sQuery(id+"F0.wireOp",EDGE,"E1.42.0.0")}),1.0]])]});
            var Q7;
            Q7=makeQuery(id+"F0.imprint","IMPRINT",FACE,{"disambiguationData":[TD([[makeQuery(id+"F0.imprint","IMPRINT",EDGE,{"derivedFrom":sQuery(id+"F0.wireOp",EDGE,"E1.58.0.0")}),1.0]])]});
            var Q8;
            Q8=makeQuery(id+"F0.imprint","IMPRINT",FACE,{"disambiguationData":[TD([[makeQuery(id+"F0.imprint","IMPRINT",EDGE,{"derivedFrom":sQuery(id+"F0.wireOp",EDGE,"E1.31.0.0")}),1.0]])]});
            var Q9;
            Q9=makeQuery(id+"F0.imprint","IMPRINT",FACE,{"disambiguationData":[TD([[makeQuery(id+"F0.imprint","IMPRINT",EDGE,{"derivedFrom":sQuery(id+"F0.wireOp",EDGE,"E1.47.0.0")}),1.0]])]});
            var Q10;
            Q10=makeQuery(id+"F0.imprint","IMPRINT",FACE,{"disambiguationData":[TD([[makeQuery(id+"F0.imprint","IMPRINT",EDGE,{"derivedFrom":sQuery(id+"F0.wireOp",EDGE,"E1.45.0.0")}),1.0]])]});
            var Q11;
            Q11=makeQuery(id+"F0.imprint","IMPRINT",FACE,{"disambiguationData":[TD([[makeQuery(id+"F0.imprint","IMPRINT",EDGE,{"derivedFrom":sQuery(id+"F0.wireOp",EDGE,"E1.29.0.0")}),1.0]])]});
            var Q12;
            Q12=makeQuery(id+"F0.imprint","IMPRINT",FACE,{"disambiguationData":[TD([[makeQuery(id+"F0.imprint","IMPRINT",EDGE,{"derivedFrom":sQuery(id+"F0.wireOp",EDGE,"E1.46.0.0")}),1.0]])]});
            var Q13;
            Q13=makeQuery(id+"F0.imprint","IMPRINT",FACE,{"disambiguationData":[TD([[makeQuery(id+"F0.imprint","IMPRINT",EDGE,{"derivedFrom":sQuery(id+"F0.wireOp",EDGE,"E1.30.0.0")}),1.0]])]});
            var Q14;
            Q14=makeQuery(id+"F0.imprint","IMPRINT",FACE,{"disambiguationData":[TD([[makeQuery(id+"F0.imprint","IMPRINT",EDGE,{"derivedFrom":sQuery(id+"F0.wireOp",EDGE,"E1.16.0.0")}),1.0]])]});
            var Q15;
            Q15=makeQuery(id+"F0.imprint","IMPRINT",FACE,{"disambiguationData":[TD([[makeQuery(id+"F0.imprint","IMPRINT",EDGE,{"derivedFrom":sQuery(id+"F0.wireOp",EDGE,"E1.48.0.0")}),1.0]])]});
            var Q16;
            Q16=makeQuery(id+"F0.imprint","IMPRINT",FACE,{"disambiguationData":[TD([[makeQuery(id+"F0.imprint","IMPRINT",EDGE,{"derivedFrom":sQuery(id+"F0.wireOp",EDGE,"E1.32.0.0")}),1.0]])]});
            var Q17;
            Q17=makeQuery(id+"F0.imprint","IMPRINT",FACE,{"disambiguationData":[TD([[makeQuery(id+"F0.imprint","IMPRINT",EDGE,{"derivedFrom":sQuery(id+"F0.wireOp",EDGE,"E1.17.0.0")}),1.0]])]});
            var Q18;
            Q18=makeQuery(id+"F0.imprint","IMPRINT",FACE,{"disambiguationData":[TD([[makeQuery(id+"F0.imprint","IMPRINT",EDGE,{"derivedFrom":sQuery(id+"F0.wireOp",EDGE,"E1.49.0.0")}),1.0]])]});
            var Q19;
            Q19=makeQuery(id+"F0.imprint","IMPRINT",FACE,{"disambiguationData":[TD([[makeQuery(id+"F0.imprint","IMPRINT",EDGE,{"derivedFrom":sQuery(id+"F0.wireOp",EDGE,"E1.33.0.0")}),1.0]])]});
            var Q20;
            Q20=makeQuery(id+"F0.imprint","IMPRINT",FACE,{"disambiguationData":[TD([[makeQuery(id+"F0.imprint","IMPRINT",EDGE,{"derivedFrom":sQuery(id+"F0.wireOp",EDGE,"E1.18.0.0")}),1.0]])]});
            var Q21;
            Q21=makeQuery(id+"F0.imprint","IMPRINT",FACE,{"disambiguationData":[TD([[makeQuery(id+"F0.imprint","IMPRINT",EDGE,{"derivedFrom":sQuery(id+"F0.wireOp",EDGE,"E1.50.0.0")}),1.0]])]});
            var Q22;
            Q22=makeQuery(id+"F0.imprint","IMPRINT",FACE,{"disambiguationData":[TD([[makeQuery(id+"F0.imprint","IMPRINT",EDGE,{"derivedFrom":sQuery(id+"F0.wireOp",EDGE,"E1.34.0.0")}),1.0]])]});
            var Q23;
            Q23=makeQuery(id+"F0.imprint","IMPRINT",FACE,{"disambiguationData":[TD([[makeQuery(id+"F0.imprint","IMPRINT",EDGE,{"derivedFrom":sQuery(id+"F0.wireOp",EDGE,"E1.19.0.0")}),1.0]])]});
            var Q24;
            Q24=makeQuery(id+"F0.imprint","IMPRINT",FACE,{"disambiguationData":[TD([[makeQuery(id+"F0.imprint","IMPRINT",EDGE,{"derivedFrom":sQuery(id+"F0.wireOp",EDGE,"E1.51.0.0")}),1.0]])]});
            var Q25;
            Q25=makeQuery(id+"F0.imprint","IMPRINT",FACE,{"disambiguationData":[TD([[makeQuery(id+"F0.imprint","IMPRINT",EDGE,{"derivedFrom":sQuery(id+"F0.wireOp",EDGE,"E1.35.0.0")}),1.0]])]});
            var Q26;
            Q26=makeQuery(id+"F0.imprint","IMPRINT",FACE,{"disambiguationData":[TD([[makeQuery(id+"F0.imprint","IMPRINT",EDGE,{"derivedFrom":sQuery(id+"F0.wireOp",EDGE,"E1.20.0.0")}),1.0]])]});
            var Q27;
            Q27=makeQuery(id+"F0.imprint","IMPRINT",FACE,{"disambiguationData":[TD([[makeQuery(id+"F0.imprint","IMPRINT",EDGE,{"derivedFrom":sQuery(id+"F0.wireOp",EDGE,"E1.52.0.0")}),1.0]])]});
            var Q28;
            Q28=makeQuery(id+"F0.imprint","IMPRINT",FACE,{"disambiguationData":[TD([[makeQuery(id+"F0.imprint","IMPRINT",EDGE,{"derivedFrom":sQuery(id+"F0.wireOp",EDGE,"E1.36.0.0")}),1.0]])]});
            var Q29;
            Q29=makeQuery(id+"F0.imprint","IMPRINT",FACE,{"disambiguationData":[TD([[makeQuery(id+"F0.imprint","IMPRINT",EDGE,{"derivedFrom":sQuery(id+"F0.wireOp",EDGE,"E1.21.0.0")}),1.0]])]});
            var Q30;
            Q30=makeQuery(id+"F0.imprint","IMPRINT",FACE,{"disambiguationData":[TD([[makeQuery(id+"F0.imprint","IMPRINT",EDGE,{"derivedFrom":sQuery(id+"F0.wireOp",EDGE,"E1.53.0.0")}),1.0]])]});
            var Q31;
            Q31=makeQuery(id+"F0.imprint","IMPRINT",FACE,{"disambiguationData":[TD([[makeQuery(id+"F0.imprint","IMPRINT",EDGE,{"derivedFrom":sQuery(id+"F0.wireOp",EDGE,"E1.37.0.0")}),1.0]])]});
            var Q32;
            Q32=makeQuery(id+"F0.imprint","IMPRINT",FACE,{"disambiguationData":[TD([[makeQuery(id+"F0.imprint","IMPRINT",EDGE,{"derivedFrom":sQuery(id+"F0.wireOp",EDGE,"E1.54.0.0")}),1.0]])]});
            var Q33;
            Q33=makeQuery(id+"F0.imprint","IMPRINT",FACE,{"disambiguationData":[TD([[makeQuery(id+"F0.imprint","IMPRINT",EDGE,{"derivedFrom":sQuery(id+"F0.wireOp",EDGE,"E1.38.0.0")}),1.0]])]});
            var Q34;
            Q34=makeQuery(id+"F0.imprint","IMPRINT",FACE,{"disambiguationData":[TD([[makeQuery(id+"F0.imprint","IMPRINT",EDGE,{"derivedFrom":sQuery(id+"F0.wireOp",EDGE,"E1.22.0.0")}),1.0]])]});
            var Q35;
            Q35=makeQuery(id+"F0.imprint","IMPRINT",FACE,{"disambiguationData":[TD([[makeQuery(id+"F0.imprint","IMPRINT",EDGE,{"derivedFrom":sQuery(id+"F0.wireOp",EDGE,"E1.15.0.0")}),1.0]])]});
            var Q36;
            Q36=makeQuery(id+"F0.imprint","IMPRINT",FACE,{"disambiguationData":[TD([[makeQuery(id+"F0.imprint","IMPRINT",EDGE,{"derivedFrom":sQuery(id+"F0.wireOp",EDGE,"E1.13.0.0")}),1.0]])]});
            var Q37;
            Q37=makeQuery(id+"F0.imprint","IMPRINT",FACE,{"disambiguationData":[TD([[makeQuery(id+"F0.imprint","IMPRINT",EDGE,{"derivedFrom":sQuery(id+"F0.wireOp",EDGE,"E1.14.0.0")}),1.0]])]});
            var Q38;
            Q38=makeQuery(id+"F0.imprint","IMPRINT",FACE,{"disambiguationData":[TD([[makeQuery(id+"F0.imprint","IMPRINT",EDGE,{"derivedFrom":sQuery(id+"F0.wireOp",EDGE,"E0.bottom")}),1.0]])]});
            var Q39;
            Q39=makeQuery(id+"F0.imprint","IMPRINT",FACE,{"disambiguationData":[TD([[makeQuery(id+"F0.imprint","IMPRINT",EDGE,{"derivedFrom":sQuery(id+"F0.wireOp",EDGE,"E1.1.0.0")}),1.0]])]});
            var Q40;
            Q40=makeQuery(id+"F0.imprint","IMPRINT",FACE,{"disambiguationData":[TD([[makeQuery(id+"F0.imprint","IMPRINT",EDGE,{"derivedFrom":sQuery(id+"F0.wireOp",EDGE,"E1.2.0.0")}),1.0]])]});
            var Q41;
            Q41=makeQuery(id+"F0.imprint","IMPRINT",FACE,{"disambiguationData":[TD([[makeQuery(id+"F0.imprint","IMPRINT",EDGE,{"derivedFrom":sQuery(id+"F0.wireOp",EDGE,"E1.3.0.0")}),1.0]])]});
            var Q42;
            Q42=makeQuery(id+"F0.imprint","IMPRINT",FACE,{"disambiguationData":[TD([[makeQuery(id+"F0.imprint","IMPRINT",EDGE,{"derivedFrom":sQuery(id+"F0.wireOp",EDGE,"E1.4.0.0")}),1.0]])]});
            var Q43;
            Q43=makeQuery(id+"F0.imprint","IMPRINT",FACE,{"disambiguationData":[TD([[makeQuery(id+"F0.imprint","IMPRINT",EDGE,{"derivedFrom":sQuery(id+"F0.wireOp",EDGE,"E1.5.0.0")}),1.0]])]});
            var Q44;
            Q44=makeQuery(id+"F0.imprint","IMPRINT",FACE,{"disambiguationData":[TD([[makeQuery(id+"F0.imprint","IMPRINT",EDGE,{"derivedFrom":sQuery(id+"F0.wireOp",EDGE,"E1.6.0.0")}),1.0]])]});
            var Q45;
            Q45=makeQuery(id+"F0.imprint","IMPRINT",FACE,{"disambiguationData":[TD([[makeQuery(id+"F0.imprint","IMPRINT",EDGE,{"derivedFrom":sQuery(id+"F0.wireOp",EDGE,"E1.7.0.0")}),1.0]])]});
            var Q46;
            Q46=makeQuery(id+"F0.imprint","IMPRINT",FACE,{"disambiguationData":[TD([[makeQuery(id+"F0.imprint","IMPRINT",EDGE,{"derivedFrom":sQuery(id+"F0.wireOp",EDGE,"E1.8.0.0")}),1.0]])]});
            var Q47;
            Q47=makeQuery(id+"F0.imprint","IMPRINT",FACE,{"disambiguationData":[TD([[makeQuery(id+"F0.imprint","IMPRINT",EDGE,{"derivedFrom":sQuery(id+"F0.wireOp",EDGE,"E1.9.0.0")}),1.0]])]});
            var Q48;
            Q48=makeQuery(id+"F0.imprint","IMPRINT",FACE,{"disambiguationData":[TD([[makeQuery(id+"F0.imprint","IMPRINT",EDGE,{"derivedFrom":sQuery(id+"F0.wireOp",EDGE,"E1.10.0.0")}),1.0]])]});
            var Q49;
            Q49=makeQuery(id+"F0.imprint","IMPRINT",FACE,{"disambiguationData":[TD([[makeQuery(id+"F0.imprint","IMPRINT",EDGE,{"derivedFrom":sQuery(id+"F0.wireOp",EDGE,"E1.11.0.0")}),1.0]])]});
            var Q50;
            Q50=makeQuery(id+"F0.imprint","IMPRINT",FACE,{"disambiguationData":[TD([[makeQuery(id+"F0.imprint","IMPRINT",EDGE,{"derivedFrom":sQuery(id+"F0.wireOp",EDGE,"E1.12.0.0")}),1.0]])]});
            var Q51;
            Q51=makeQuery(id+"F0.imprint","IMPRINT",FACE,{"disambiguationData":[TD([[makeQuery(id+"F0.imprint","IMPRINT",EDGE,{"derivedFrom":sQuery(id+"F0.wireOp",EDGE,"E1.55.0.0")}),1.0]])]});
            var Q52;
            Q52=makeQuery(id+"F0.imprint","IMPRINT",FACE,{"disambiguationData":[TD([[makeQuery(id+"F0.imprint","IMPRINT",EDGE,{"derivedFrom":sQuery(id+"F0.wireOp",EDGE,"E1.39.0.0")}),1.0]])]});
            var Q53;
            Q53=makeQuery(id+"F0.imprint","IMPRINT",FACE,{"disambiguationData":[TD([[makeQuery(id+"F0.imprint","IMPRINT",EDGE,{"derivedFrom":sQuery(id+"F0.wireOp",EDGE,"E1.23.0.0")}),1.0]])]});
            var Q54;
            Q54=makeQuery(id+"F0.imprint","IMPRINT",FACE,{"disambiguationData":[TD([[makeQuery(id+"F0.imprint","IMPRINT",EDGE,{"derivedFrom":sQuery(id+"F0.wireOp",EDGE,"E1.56.0.0")}),1.0]])]});
            var Q55;
            Q55=makeQuery(id+"F0.imprint","IMPRINT",FACE,{"disambiguationData":[TD([[makeQuery(id+"F0.imprint","IMPRINT",EDGE,{"derivedFrom":sQuery(id+"F0.wireOp",EDGE,"E1.40.0.0")}),1.0]])]});
            var Q56;
            Q56=makeQuery(id+"F0.imprint","IMPRINT",FACE,{"disambiguationData":[TD([[makeQuery(id+"F0.imprint","IMPRINT",EDGE,{"derivedFrom":sQuery(id+"F0.wireOp",EDGE,"E1.24.0.0")}),1.0]])]});
            var Q57;
            Q57=makeQuery(id+"F0.imprint","IMPRINT",FACE,{"disambiguationData":[TD([[makeQuery(id+"F0.imprint","IMPRINT",EDGE,{"derivedFrom":sQuery(id+"F0.wireOp",EDGE,"E1.57.0.0")}),1.0]])]});
            var Q58;
            Q58=makeQuery(id+"F0.imprint","IMPRINT",FACE,{"disambiguationData":[TD([[makeQuery(id+"F0.imprint","IMPRINT",EDGE,{"derivedFrom":sQuery(id+"F0.wireOp",EDGE,"E1.41.0.0")}),1.0]])]});
            var Q59;
            Q59=makeQuery(id+"F0.imprint","IMPRINT",FACE,{"disambiguationData":[TD([[makeQuery(id+"F0.imprint","IMPRINT",EDGE,{"derivedFrom":sQuery(id+"F0.wireOp",EDGE,"E1.25.0.0")}),1.0]])]});
            extrude(context, id + "F1", {"entities" : qUnion([Q0, Q1, Q2, Q3, Q4, Q5, Q6, Q7, Q8, Q9, Q10, Q11, Q12, Q13, Q14, Q15, Q16, Q17, Q18, Q19, Q20, Q21, Q22, Q23, Q24, Q25, Q26, Q27, Q28, Q29, Q30, Q31, Q32, Q33, Q34, Q35, Q36, Q37, Q38, Q39, Q40, Q41, Q42, Q43, Q44, Q45, Q46, Q47, Q48, Q49, Q50, Q51, Q52, Q53, Q54, Q55, Q56, Q57, Q58, Q59]), "depth" : 0.5 * mm, "offsetDistance" : 25 * mm});
        }
    });
